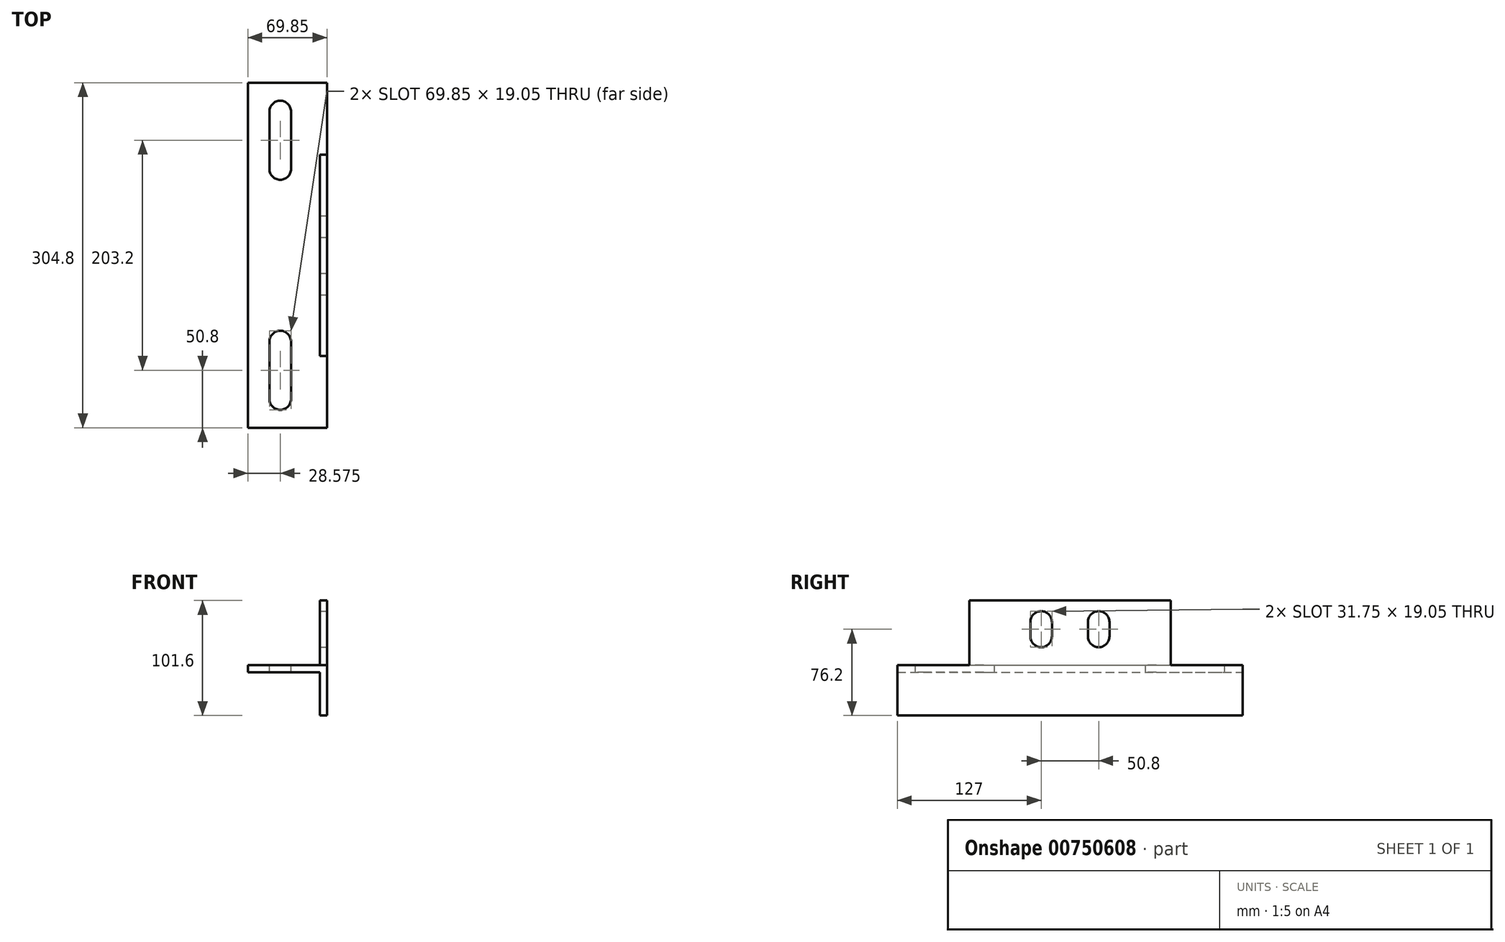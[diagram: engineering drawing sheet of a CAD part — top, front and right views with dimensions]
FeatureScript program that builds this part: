
annotation { "Feature Type Name" : "Feature", "Feature Type Description" : "" }
export const myFeature = defineFeature(function(context is Context, id is Id, definition is map)
    precondition{}
    {
        {
            var Q0;
            Q0=qCreatedBy(makeId("Front.planeOp"),FACE);
            var sketch = newSketch(context, id + "F0", { "sketchPlane" : qUnion([Q0])});
            skLineSegment(sketch, "E0.bottom", {"start": v(0, 0) * mm, "end": v(6.35, 0) * mm});
            skLineSegment(sketch, "E0.top", {"start": v(0, 101.6) * mm, "end": v(6.35, 101.6) * mm});
            skLineSegment(sketch, "E0.left", {"start": v(0, 0) * mm, "end": v(0, 38.1) * mm});
            skLineSegment(sketch, "E1.bottom", {"start": v(0, 38.1) * mm, "end": v(-63.5, 38.1) * mm});
            skLineSegment(sketch, "E1.top", {"start": v(0, 44.45) * mm, "end": v(-63.5, 44.45) * mm});
            skLineSegment(sketch, "E1.right", {"start": v(-63.5, 38.1) * mm, "end": v(-63.5, 44.45) * mm});
            skLineSegment(sketch, "E2.trimOffspring", {"start": v(0, 44.45) * mm, "end": v(0, 101.6) * mm});
            skLineSegment(sketch, "E3.trimOffspring", {"start": v(6.35, 0) * mm, "end": v(6.35, 101.6) * mm});
            skSolve(sketch);
        }
        {
            var Q0;
            Q0 = qSketchRegion(id + "F0", true);
            extrude(context, id + "F1", {"entities" : qUnion([Q0]), "depth" : 304.8 * mm, "offsetDistance" : 25.4 * mm});
        }
        {
            var Q0;
            Q0=makeQuery(id+"F1.opExtrude","SWEPT_FACE",FACE,{"disambiguationData":[OSD([sQuery(id+"F0.wireOp",EDGE,"E3.trimOffspring")])]});
            var sketch = newSketch(context, id + "F2", { "sketchPlane" : qUnion([Q0])});
            skLineSegment(sketch, "E4.bottom", {"start": v(-304.8, 101.6) * mm, "end": v(-241.3, 101.6) * mm});
            skLineSegment(sketch, "E4.top", {"start": v(-304.8, 44.45) * mm, "end": v(-241.3, 44.45) * mm});
            skLineSegment(sketch, "E4.left", {"start": v(-304.8, 101.6) * mm, "end": v(-304.8, 44.45) * mm});
            skLineSegment(sketch, "E4.right", {"start": v(-241.3, 101.6) * mm, "end": v(-241.3, 44.45) * mm});
            skLineSegment(sketch, "E5", {"start": v(-152.4, 101.6) * mm, "end": v(-152.4, 0) * mm, "construction": true});
            skPoint(sketch, "E5.endSnap0", {"position": v(-152.4, 0) * mm});
            skLineSegment(sketch, "E6.MirrorCS", {"start": v(0, 44.45) * mm, "end": v(-63.5, 44.45) * mm});
            skLineSegment(sketch, "E7.MirrorCS", {"start": v(0, 101.6) * mm, "end": v(-63.5, 101.6) * mm});
            skLineSegment(sketch, "E8.MirrorCS", {"start": v(0, 101.6) * mm, "end": v(0, 44.45) * mm});
            skLineSegment(sketch, "E9.MirrorCS", {"start": v(-63.5, 101.6) * mm, "end": v(-63.5, 44.45) * mm});
            skLineSegment(sketch, "E10.left", {"start": v(-168.28, 82.55) * mm, "end": v(-168.28, 69.85) * mm});
            skLineSegment(sketch, "E10.right", {"start": v(-187.33, 82.55) * mm, "end": v(-187.33, 69.85) * mm});
            skArc(sketch, "E11", {"start": v(-168.28, 82.55) * mm, "mid": v(-177.8, 92.08) * mm, "end": v(-187.33, 82.55) * mm});
            skArc(sketch, "E12", {"start": v(-187.33, 69.85) * mm, "mid": v(-177.8, 60.33) * mm, "end": v(-168.28, 69.85) * mm});
            skArc(sketch, "E13.MirrorCS", {"start": v(-136.53, 82.55) * mm, "mid": v(-127, 92.08) * mm, "end": v(-117.48, 82.55) * mm});
            skLineSegment(sketch, "E14.MirrorCS", {"start": v(-136.53, 82.55) * mm, "end": v(-136.53, 69.85) * mm});
            skArc(sketch, "E15.MirrorCS", {"start": v(-117.48, 69.85) * mm, "mid": v(-127, 60.33) * mm, "end": v(-136.53, 69.85) * mm});
            skLineSegment(sketch, "E16.MirrorCS", {"start": v(-117.48, 82.55) * mm, "end": v(-117.48, 69.85) * mm});
            skSolve(sketch);
        }
        {
            var Q0;
            Q0 = qSketchRegion(id + "F2", true);
            extrude(context, id + "F3", {"entities" : qUnion([Q0]), "operationType" : NewBodyOperationType.REMOVE, "endBound" : BoundingType.UP_TO_NEXT, "oppositeDirection" : true, "depth" : 25.4 * mm, "offsetDistance" : 25.4 * mm});
        }
        {
            var Q0;
            Q0=makeQuery(id+"F3.boolean.opBoolean","MERGE",FACE,{"derivedFrom":[makeQuery(id+"F1.opExtrude","SWEPT_FACE",FACE,{"disambiguationData":[OSD([sQuery(id+"F0.wireOp",EDGE,"E1.top")])]}),makeQuery(id+"F3.opExtrude","SWEPT_FACE",FACE,{"disambiguationData":[OSD([sQuery(id+"F2.wireOp",EDGE,"E4.top")])]}),makeQuery(id+"F3.opExtrude","SWEPT_FACE",FACE,{"disambiguationData":[OSD([sQuery(id+"F2.wireOp",EDGE,"E6.MirrorCS")])]})]});
            var sketch = newSketch(context, id + "F4", { "sketchPlane" : qUnion([Q0])});
            skLineSegment(sketch, "E17.left", {"start": v(-25.4, -228.6) * mm, "end": v(-25.4, -279.4) * mm});
            skLineSegment(sketch, "E17.right", {"start": v(-44.45, -228.6) * mm, "end": v(-44.45, -279.4) * mm});
            skArc(sketch, "E18", {"start": v(-25.4, -228.6) * mm, "mid": v(-34.93, -219.08) * mm, "end": v(-44.45, -228.6) * mm});
            skArc(sketch, "E19", {"start": v(-44.45, -279.4) * mm, "mid": v(-34.93, -288.93) * mm, "end": v(-25.4, -279.4) * mm});
            skLineSegment(sketch, "E20", {"start": v(-63.5, -152.4) * mm, "end": v(0, -152.4) * mm, "construction": true});
            skLineSegment(sketch, "E21.MirrorCS", {"start": v(-25.4, -76.2) * mm, "end": v(-25.4, -25.4) * mm});
            skLineSegment(sketch, "E22.MirrorCS", {"start": v(-44.45, -76.2) * mm, "end": v(-44.45, -25.4) * mm});
            skArc(sketch, "E23.MirrorCS", {"start": v(-25.4, -76.2) * mm, "mid": v(-34.92, -85.73) * mm, "end": v(-44.45, -76.2) * mm});
            skArc(sketch, "E24.MirrorCS", {"start": v(-44.45, -25.4) * mm, "mid": v(-34.92, -15.88) * mm, "end": v(-25.4, -25.4) * mm});
            skSolve(sketch);
        }
        {
            var Q0;
            Q0 = qSketchRegion(id + "F4", true);
            extrude(context, id + "F5", {"entities" : qUnion([Q0]), "operationType" : NewBodyOperationType.REMOVE, "endBound" : BoundingType.UP_TO_NEXT, "oppositeDirection" : true, "depth" : 25.4 * mm, "offsetDistance" : 25.4 * mm});
        }
    });
